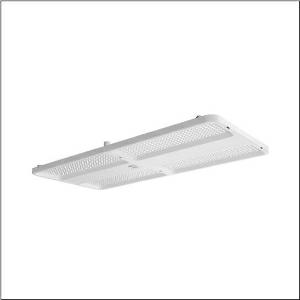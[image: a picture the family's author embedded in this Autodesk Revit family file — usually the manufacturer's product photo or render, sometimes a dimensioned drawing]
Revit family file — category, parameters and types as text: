
# Revit family: highbay_21_maxi_52hn12db4qda01
name_source: partatom
category: Lighting Fixtures
units: mm (PartAtom-declared; Revit-internal decimal feet)

## family parameters
Cut with Voids When Loaded = No
Host = Face
Light Source = No
Part Type = Normal
Room Calculation Point = No
Round Connector Dimension = Use Diameter
Shared = No

## types (1)
- --- (1 x LED, 38000 lm, 198.2 W, 4000K)
    Apparent Load = 198 VA
    CIE Flux Codes = 90 98 100 100 100
    Color Rendering = 80
    Color Temperature = 4000K
    Default Elevation = 1800 mm
    Description = high bay luminaire Highbay 21 maxi; direct symmetric wide distribution, light control with lens of PMMA; UGR ≤ 22 (X = 4H | Y = 8H | S = 0.25H | reflection values 70/50/20); luminous flux: 38.000lm; light colour: 840, colour temperature: 4000K, MacAdam ≤ 3 SDCM (initial), colour rendering: CRI > 80; luminous efficacy: 191,7lm/W; rated service life: 75.000h (L80/B50) at AT= ta max; control: Bluetooth® Mesh; for wireless networking: Node multi-sensor luminaire for setting up a local control solution without a higher-level application controller, intelligence completely integrated into the luminaire; with auto-swarm function: leading lighting creates safety. The function is already active without any „out-of-the-box“ commissioning; commissioning is not necessary thanks to „out-of-the-box“ functions: basic functions (presence lighting, follow-up times, fading times, etc.) are already preset at the factory; no control line such as DALI between the Node multi-sensor luminaires and Nodes is required, wireless integration of other Node luminaires and Node multi-sensor luminaires into the network is possible; number of Node multi-sensor luminaires in the project can be expanded as required, network sizes > 300 Nodes can be realized; can also be connected to lighting or building automation via various gateways upon request; integrated DALI2 ECG provides luminaire data (according to IEC62386, Part 251), energy data (Part 252), and monitoring and analytics data (Part 253) to higher-level systems for further processing; luminaire with PIR sensor (passive-infrared); with light sensor; luminaire connection: terminal, 5-pole, max. 2.5mm² (cable entry for one cable, Ø 8.5..16mm); mains connection: 230..240V, AC 50/60Hz; connected load: 198,2W; protection rating (complete): IP65; insulation class (complete): insulation class I (protective earthing); protection symbol: D; certification: CE, ENEC, VDE, UKCA; internal wiring halogen-free; luminaire corresponds to IFS (International Featured Standards) requirements for safety and quality in the food industry; LABS conformity tested according to VDMA 24364:2018-05; housing frame of high-performance plastic PA6, matt traffic white (RAL 9016); cover of PMMA; dimension (LxWxH): 946 x 442 x 72mm; permissible operating ambient temperature: -20..+40°C (reducing of maximum allowable ambient temperature of 5°C with ceiling mounting); packaging unit: 1 piece; (delivery without accessories; please order mounting accessories separately)
    Height = 72 mm  [stored 0.23622 ft]
    Lamp = 1 x LED
    Lamp Light Flux = 38000 lm
    Lamp Power = 198.2 W
    Lamp count = 1
    Length = 946 mm
    Luminous efficacy = 192 lm/W
    Manufacturer = Siteco
    ModVariant = No
    Model = 52HN12DB4QDA01
    Mounting Place = Ceiling
    Mounting Type = Pendant
    Number of Poles = 1
    OnlyDefault = Yes
    Power Factor = 1
    Product Name = Highbay 21 maxi
    Product group = high bay luminaire
    ProductGroupID = 901
    Protection Class = Protection class I
    Protection Degree = IP 65
    RLX_Detail_Level = 1
    RLX_Emergency_Light_Flux = 0 lm
    RLX_Emergency_Type = 0
    RLX_Emergency_Type_DB = No
    RlxData = <blob elided: 129005 chars, md5=f28f6aee>
    Socket = socket
    Standby Power = 0 W
    System Light Flux = 38001 lm
    System Power = 198 W
    Type Comments = factory setting: luminous flux: 100 % | dim-lin: 254 | 918 mA
    Type Image = l_1363267.jpg
    URL = http://relux.com
    VarID = @adj_012039
    Voltage = 0 V
    Weight = 0.00 kg
    Width = 442 mm

note: [stored X ft] marks values corroborated as IEEE doubles in the binary element streams (Revit-internal decimal feet)

## geometry (parser evidence)
native form markers: Blend x4, Sweep x9
no freeform markers — native parametric forms only
